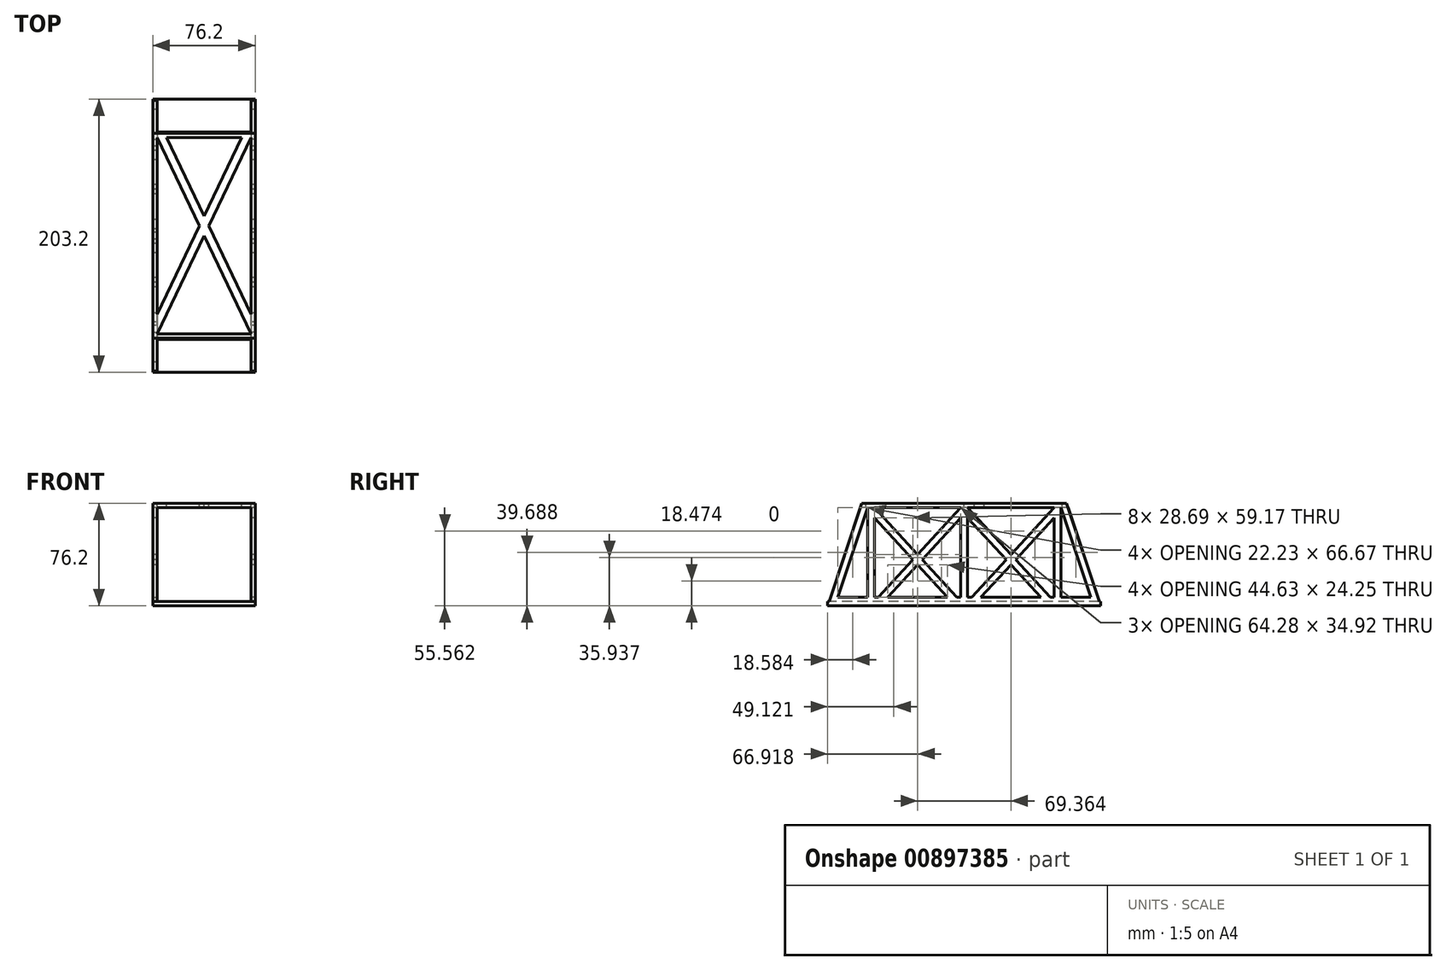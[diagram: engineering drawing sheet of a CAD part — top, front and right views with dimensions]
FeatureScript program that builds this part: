
annotation { "Feature Type Name" : "Feature", "Feature Type Description" : "" }
export const myFeature = defineFeature(function(context is Context, id is Id, definition is map)
    precondition{}
    {
        {
            var Q0;
            Q0=qCreatedBy(makeId("Right.planeOp"),FACE);
            var sketch = newSketch(context, id + "F0", { "sketchPlane" : qUnion([Q0])});
            skLineSegment(sketch, "E0", {"start": v(-101.6, -38.1) * mm, "end": v(101.6, -38.1) * mm});
            skLineSegment(sketch, "E1", {"start": v(101.6, -38.1) * mm, "end": v(76.2, 38.1) * mm});
            skLineSegment(sketch, "E2", {"start": v(76.2, 38.1) * mm, "end": v(-76.2, 38.1) * mm});
            skLineSegment(sketch, "E3", {"start": v(-76.2, 38.1) * mm, "end": v(-101.6, -38.1) * mm});
            skSolve(sketch);
        }
        {
            var Q0;
            Q0 = qSketchRegion(id + "F0", true);
            extrude(context, id + "F1", {"entities" : qUnion([Q0]), "endBound" : BoundingType.SYMMETRIC, "depth" : 76.2 * mm, "offsetDistance" : 25.4 * mm});
        }
        {
            var Q0;
            Q0=qCreatedBy(makeId("Front.planeOp"),FACE);
            var sketch = newSketch(context, id + "F2", { "sketchPlane" : qUnion([Q0])});
            skLineSegment(sketch, "E4.bottom", {"start": v(34.92, -34.93) * mm, "end": v(-34.93, -34.93) * mm});
            skLineSegment(sketch, "E4.top", {"start": v(34.92, 34.93) * mm, "end": v(-34.93, 34.92) * mm});
            skLineSegment(sketch, "E4.left", {"start": v(34.92, -34.93) * mm, "end": v(34.92, 34.92) * mm});
            skLineSegment(sketch, "E4.right", {"start": v(-34.93, -34.93) * mm, "end": v(-34.93, 34.92) * mm});
            skPoint(sketch, "E4.middle", {"position": v(0, 0) * mm});
            skSolve(sketch);
        }
        {
            var Q0;
            Q0 = qSketchRegion(id + "F2", true);
            extrude(context, id + "F3", {"entities" : qUnion([Q0]), "operationType" : NewBodyOperationType.REMOVE, "endBound" : BoundingType.SYMMETRIC, "oppositeDirection" : true, "depth" : 254 * mm, "offsetDistance" : 25.4 * mm});
        }
        {
            var Q0;
            Q0=makeQuery(id+"F1.opExtrude","CAP_FACE",FACE,{"disambiguationData":[OSD([sQuery(id+"F0.wireOp",EDGE,"E0"),sQuery(id+"F0.wireOp",EDGE,"E1"),sQuery(id+"F0.wireOp",EDGE,"E2"),sQuery(id+"F0.wireOp",EDGE,"E3")])],"isStart":true});
            var sketch = newSketch(context, id + "F4", { "sketchPlane" : qUnion([Q0])});
            skLineSegment(sketch, "E5", {"start": v(-95.19, -34.93) * mm, "end": v(-71.9, 34.93) * mm});
            skLineSegment(sketch, "E6", {"start": v(-71.9, 34.93) * mm, "end": v(-71.9, -34.92) * mm});
            skLineSegment(sketch, "E7", {"start": v(-71.9, -34.92) * mm, "end": v(-95.19, -34.92) * mm});
            skLineSegment(sketch, "E8.MirrorCS", {"start": v(71.9, 34.93) * mm, "end": v(71.9, -34.92) * mm});
            skLineSegment(sketch, "E9.MirrorCS", {"start": v(71.9, -34.92) * mm, "end": v(95.19, -34.92) * mm});
            skLineSegment(sketch, "E10.MirrorCS", {"start": v(95.19, -34.93) * mm, "end": v(71.9, 34.93) * mm});
            skLineSegment(sketch, "E11", {"start": v(-71.9, 34.93) * mm, "end": v(71.9, 34.93) * mm});
            skLineSegment(sketch, "E12", {"start": v(-71.9, -34.92) * mm, "end": v(71.9, -34.92) * mm});
            skLineSegment(sketch, "E13", {"start": v(-66.82, 34.93) * mm, "end": v(-66.82, -34.93) * mm});
            skLineSegment(sketch, "E14", {"start": v(66.82, 34.93) * mm, "end": v(66.82, -34.92) * mm});
            skLineSegment(sketch, "E15.bottom", {"start": v(2.54, -34.93) * mm, "end": v(-2.54, -34.93) * mm});
            skLineSegment(sketch, "E15.top", {"start": v(2.54, 34.93) * mm, "end": v(-2.54, 34.93) * mm});
            skLineSegment(sketch, "E15.left", {"start": v(2.54, -34.93) * mm, "end": v(2.54, 34.93) * mm});
            skLineSegment(sketch, "E15.right", {"start": v(-2.54, -34.93) * mm, "end": v(-2.54, 34.93) * mm});
            skPoint(sketch, "E15.middle", {"position": v(0, 0) * mm});
            skLineSegment(sketch, "E16", {"start": v(-66.82, 34.93) * mm, "end": v(-2.54, -34.93) * mm});
            skLineSegment(sketch, "E17", {"start": v(66.82, 34.93) * mm, "end": v(2.54, -34.93) * mm});
            skLineSegment(sketch, "E18", {"start": v(-66.82, 27.42) * mm, "end": v(-9.44, -34.93) * mm});
            skLineSegment(sketch, "E19", {"start": v(66.82, 27.42) * mm, "end": v(9.44, -34.93) * mm});
            skLineSegment(sketch, "E20", {"start": v(-2.54, 34.93) * mm, "end": v(-66.82, -34.93) * mm});
            skLineSegment(sketch, "E21", {"start": v(-2.54, 27.42) * mm, "end": v(-59.92, -34.93) * mm});
            skLineSegment(sketch, "E22.MirrorCS", {"start": v(2.54, 34.93) * mm, "end": v(66.82, -34.93) * mm});
            skLineSegment(sketch, "E23.MirrorCS", {"start": v(2.54, 27.42) * mm, "end": v(59.92, -34.93) * mm});
            skSolve(sketch);
        }
        {
            var Q0;
            Q0=makeQuery(id+"F4.imprint","IMPRINT",FACE,{"disambiguationData":[TD([[makeQuery(id+"F4.imprint","IMPRINT",EDGE,{"derivedFrom":sQuery(id+"F4.wireOp",EDGE,"E5")}),-1.0]])]});
            var Q1;
            {var subQ1=sQuery(id+"F4.wireOp",EDGE,"E13");var subQ3=sQuery(id+"F4.wireOp",EDGE,"E18");var subQ4=makeQuery(id+"F4.imprint","INTERSECT",VERTEX,{"derivedFrom":[subQ1,subQ3]});Q1=makeQuery(id+"F4.imprint","IMPRINT",FACE,{"disambiguationData":[TD([[makeQuery(id+"F4.imprint","IMPRINT",EDGE,{"disambiguationData":[TD([[subQ4,-1.0]])],"derivedFrom":subQ3}),-1.0]])]});}
            var Q2;
            {var subQ0=sQuery(id+"F4.wireOp",EDGE,"E16");var subQ3=sQuery(id+"F4.wireOp",EDGE,"E20");var subQ5=makeQuery(id+"F4.imprint","INTERSECT",VERTEX,{"derivedFrom":[subQ0,subQ3]});Q2=makeQuery(id+"F4.imprint","IMPRINT",FACE,{"disambiguationData":[TD([[makeQuery(id+"F4.imprint","IMPRINT",EDGE,{"disambiguationData":[TD([[subQ5,1.0]])],"derivedFrom":subQ0}),1.0]])]});}
            var Q3;
            {var subQ1=sQuery(id+"F4.wireOp",EDGE,"E15.right");var subQ3=sQuery(id+"F4.wireOp",EDGE,"E21");var subQ4=makeQuery(id+"F4.imprint","INTERSECT",VERTEX,{"derivedFrom":[subQ1,subQ3]});Q3=makeQuery(id+"F4.imprint","IMPRINT",FACE,{"disambiguationData":[TD([[makeQuery(id+"F4.imprint","IMPRINT",EDGE,{"disambiguationData":[TD([[subQ4,-1.0]])],"derivedFrom":subQ3}),1.0]])]});}
            var Q4;
            {var subQ0=sQuery(id+"F4.wireOp",EDGE,"E18");var subQ1=sQuery(id+"F4.wireOp",EDGE,"E12");var subQ2=makeQuery(id+"F4.imprint","INTERSECT",VERTEX,{"derivedFrom":[subQ1,subQ0]});Q4=makeQuery(id+"F4.imprint","IMPRINT",FACE,{"disambiguationData":[TD([[makeQuery(id+"F4.imprint","IMPRINT",EDGE,{"disambiguationData":[TD([[subQ2,1.0]])],"derivedFrom":subQ1}),1.0]])]});}
            var Q5;
            {var subQ1=sQuery(id+"F4.wireOp",EDGE,"E15.left");var subQ3=sQuery(id+"F4.wireOp",EDGE,"E23.MirrorCS");var subQ4=makeQuery(id+"F4.imprint","INTERSECT",VERTEX,{"derivedFrom":[subQ1,subQ3]});Q5=makeQuery(id+"F4.imprint","IMPRINT",FACE,{"disambiguationData":[TD([[makeQuery(id+"F4.imprint","IMPRINT",EDGE,{"disambiguationData":[TD([[subQ4,-1.0]])],"derivedFrom":subQ3}),-1.0]])]});}
            var Q6;
            {var subQ0=sQuery(id+"F4.wireOp",EDGE,"E17");var subQ3=sQuery(id+"F4.wireOp",EDGE,"E22.MirrorCS");var subQ5=makeQuery(id+"F4.imprint","INTERSECT",VERTEX,{"derivedFrom":[subQ0,subQ3]});Q6=makeQuery(id+"F4.imprint","IMPRINT",FACE,{"disambiguationData":[TD([[makeQuery(id+"F4.imprint","IMPRINT",EDGE,{"disambiguationData":[TD([[subQ5,1.0]])],"derivedFrom":subQ0}),-1.0]])]});}
            var Q7;
            {var subQ1=sQuery(id+"F4.wireOp",EDGE,"E14");var subQ3=sQuery(id+"F4.wireOp",EDGE,"E19");var subQ4=makeQuery(id+"F4.imprint","INTERSECT",VERTEX,{"derivedFrom":[subQ1,subQ3]});Q7=makeQuery(id+"F4.imprint","IMPRINT",FACE,{"disambiguationData":[TD([[makeQuery(id+"F4.imprint","IMPRINT",EDGE,{"disambiguationData":[TD([[subQ4,-1.0]])],"derivedFrom":subQ3}),1.0]])]});}
            var Q8;
            {var subQ0=sQuery(id+"F4.wireOp",EDGE,"E19");var subQ1=sQuery(id+"F4.wireOp",EDGE,"E12");var subQ2=makeQuery(id+"F4.imprint","INTERSECT",VERTEX,{"derivedFrom":[subQ1,subQ0]});Q8=makeQuery(id+"F4.imprint","IMPRINT",FACE,{"disambiguationData":[TD([[makeQuery(id+"F4.imprint","IMPRINT",EDGE,{"disambiguationData":[TD([[subQ2,-1.0]])],"derivedFrom":subQ1}),1.0]])]});}
            var Q9;
            Q9=makeQuery(id+"F4.imprint","IMPRINT",FACE,{"disambiguationData":[TD([[makeQuery(id+"F4.imprint","IMPRINT",EDGE,{"derivedFrom":sQuery(id+"F4.wireOp",EDGE,"E8.MirrorCS")}),1.0]])]});
            extrude(context, id + "F5", {"entities" : qUnion([Q0, Q1, Q2, Q3, Q4, Q5, Q6, Q7, Q8, Q9]), "operationType" : NewBodyOperationType.REMOVE, "oppositeDirection" : true, "depth" : 76.2 * mm, "offsetDistance" : 25.4 * mm});
        }
        {
            var Q0;
            Q0=makeQuery(id+"F1.opExtrude","SWEPT_FACE",FACE,{"disambiguationData":[OSD([sQuery(id+"F0.wireOp",EDGE,"E2")])]});
            var sketch = newSketch(context, id + "F6", { "sketchPlane" : qUnion([Q0])});
            skLineSegment(sketch, "E24.bottom", {"start": v(34.92, -73.03) * mm, "end": v(-34.93, -73.03) * mm});
            skLineSegment(sketch, "E24.top", {"start": v(34.92, 73.03) * mm, "end": v(-34.92, 73.03) * mm});
            skLineSegment(sketch, "E24.left", {"start": v(34.92, -73.03) * mm, "end": v(34.93, 73.02) * mm});
            skLineSegment(sketch, "E24.right", {"start": v(-34.93, -73.03) * mm, "end": v(-34.92, 73.02) * mm});
            skPoint(sketch, "E24.middle", {"position": v(0, 0) * mm});
            skLineSegment(sketch, "E25", {"start": v(-34.92, 73.03) * mm, "end": v(34.92, -73.03) * mm});
            skLineSegment(sketch, "E26", {"start": v(34.92, 73.03) * mm, "end": v(-34.92, -73.03) * mm});
            skLineSegment(sketch, "E27", {"start": v(27.89, 73.03) * mm, "end": v(-34.93, -58.3) * mm});
            skLineSegment(sketch, "E28", {"start": v(-27.89, 73.02) * mm, "end": v(34.93, -58.3) * mm});
            skSolve(sketch);
        }
        {
            var Q0;
            {var subQ1=sQuery(id+"F6.wireOp",EDGE,"E24.right");var subQ3=sQuery(id+"F6.wireOp",EDGE,"E27");var subQ4=makeQuery(id+"F6.imprint","INTERSECT",VERTEX,{"derivedFrom":[subQ1,subQ3]});Q0=makeQuery(id+"F6.imprint","IMPRINT",FACE,{"disambiguationData":[TD([[makeQuery(id+"F6.imprint","IMPRINT",EDGE,{"disambiguationData":[TD([[subQ4,1.0]])],"derivedFrom":subQ3}),-1.0]])]});}
            var Q1;
            {var subQ0=sQuery(id+"F6.wireOp",EDGE,"E24.bottom");Q1=makeQuery(id+"F6.imprint","IMPRINT",FACE,{"disambiguationData":[TD([[makeQuery(id+"F6.imprint","IMPRINT",EDGE,{"derivedFrom":subQ0}),-1.0]])]});}
            var Q2;
            {var subQ1=sQuery(id+"F6.wireOp",EDGE,"E24.left");var subQ3=sQuery(id+"F6.wireOp",EDGE,"E28");var subQ4=makeQuery(id+"F6.imprint","INTERSECT",VERTEX,{"derivedFrom":[subQ1,subQ3]});Q2=makeQuery(id+"F6.imprint","IMPRINT",FACE,{"disambiguationData":[TD([[makeQuery(id+"F6.imprint","IMPRINT",EDGE,{"disambiguationData":[TD([[subQ4,1.0]])],"derivedFrom":subQ3}),1.0]])]});}
            var Q3;
            {var subQ0=sQuery(id+"F6.wireOp",EDGE,"E27");var subQ1=sQuery(id+"F6.wireOp",EDGE,"E24.top");var subQ2=makeQuery(id+"F6.imprint","INTERSECT",VERTEX,{"derivedFrom":[subQ1,subQ0]});Q3=makeQuery(id+"F6.imprint","IMPRINT",FACE,{"disambiguationData":[TD([[makeQuery(id+"F6.imprint","IMPRINT",EDGE,{"disambiguationData":[TD([[subQ2,-1.0]])],"derivedFrom":subQ1}),1.0]])]});}
            extrude(context, id + "F7", {"entities" : qUnion([Q0, Q1, Q2, Q3]), "operationType" : NewBodyOperationType.REMOVE, "oppositeDirection" : true, "depth" : 25.4 * mm, "offsetDistance" : 25.4 * mm});
        }
        {
            var Q0;
            {var subQ0=sQuery(id+"F4.wireOp",EDGE,"E12");Q0=makeQuery(id+"F5.boolean.opBoolean","MERGE",FACE,{"derivedFrom":[makeQuery(id+"F3.boolean.opBoolean","COPY",FACE,{"derivedFrom":makeQuery(id+"F3.opExtrude","SWEPT_FACE",FACE,{"disambiguationData":[OSD([sQuery(id+"F2.wireOp",EDGE,"E4.bottom")])]})})],"fromTools":[makeQuery(id+"F5.opExtrude","SWEPT_FACE",FACE,{"disambiguationData":[OSD([sQuery(id+"F4.wireOp",EDGE,"E7")])]}),makeQuery(id+"F5.opExtrude","SWEPT_FACE",FACE,{"disambiguationData":[OSD([sQuery(id+"F4.wireOp",EDGE,"E9.MirrorCS")])]}),makeQuery(id+"F5.opExtrude","SWEPT_FACE",FACE,{"disambiguationData":[OSD([subQ0]),TDD([makeQuery(id+"F4.imprint","IMPRINT",EDGE,{"disambiguationData":[TD([[makeQuery(id+"F4.imprint","INTERSECT",VERTEX,{"derivedFrom":[subQ0,sQuery(id+"F4.wireOp",EDGE,"E18")]}),1.0]])],"derivedFrom":subQ0})])]}),makeQuery(id+"F5.opExtrude","SWEPT_FACE",FACE,{"disambiguationData":[OSD([subQ0]),TDD([makeQuery(id+"F4.imprint","IMPRINT",EDGE,{"disambiguationData":[TD([[makeQuery(id+"F4.imprint","INTERSECT",VERTEX,{"derivedFrom":[subQ0,sQuery(id+"F4.wireOp",EDGE,"E19")]}),-1.0]])],"derivedFrom":subQ0})])]})]});}
            var sketch = newSketch(context, id + "F8", { "sketchPlane" : qUnion([Q0])});
            skLineSegment(sketch, "E29.bottom", {"start": v(-38.1, -95.19) * mm, "end": v(-34.93, -95.19) * mm});
            skLineSegment(sketch, "E29.top", {"start": v(-38.1, 95.19) * mm, "end": v(-34.93, 95.19) * mm});
            skLineSegment(sketch, "E29.left", {"start": v(-38.1, -95.19) * mm, "end": v(-38.1, 95.19) * mm});
            skLineSegment(sketch, "E29.right", {"start": v(-34.93, -95.19) * mm, "end": v(-34.93, 95.19) * mm});
            skLineSegment(sketch, "E30.MirrorCS", {"start": v(38.1, -95.19) * mm, "end": v(34.93, -95.19) * mm});
            skLineSegment(sketch, "E31.MirrorCS", {"start": v(38.1, -95.19) * mm, "end": v(38.1, 95.19) * mm});
            skLineSegment(sketch, "E32.MirrorCS", {"start": v(34.93, -95.19) * mm, "end": v(34.93, 95.19) * mm});
            skLineSegment(sketch, "E33.MirrorCS", {"start": v(38.1, 95.19) * mm, "end": v(34.93, 95.19) * mm});
            skSolve(sketch);
        }
        {
            var Q0;
            Q0 = qSketchRegion(id + "F8", true);
            extrude(context, id + "F9", {"entities" : qUnion([Q0]), "operationType" : NewBodyOperationType.ADD, "depth" : 3.17 * mm, "offsetDistance" : 25.4 * mm});
        }
        {
            var Q0;
            Q0=makeQuery(id+"F9.boolean.opBoolean","MERGE",FACE,{"derivedFrom":[makeQuery(id+"F1.opExtrude","CAP_FACE",FACE,{"disambiguationData":[OSD([sQuery(id+"F0.wireOp",EDGE,"E0"),sQuery(id+"F0.wireOp",EDGE,"E1"),sQuery(id+"F0.wireOp",EDGE,"E2"),sQuery(id+"F0.wireOp",EDGE,"E3")])],"isStart":false}),makeQuery(id+"F9.opExtrude","SWEPT_FACE",FACE,{"disambiguationData":[OSD([sQuery(id+"F8.wireOp",EDGE,"E31.MirrorCS")])]})]});
            var sketch = newSketch(context, id + "F10", { "sketchPlane" : qUnion([Q0])});
            skLineSegment(sketch, "E34.bottom", {"start": v(-101.6, -38.1) * mm, "end": v(-97.33, -38.1) * mm});
            skLineSegment(sketch, "E34.top", {"start": v(-101.6, -34.93) * mm, "end": v(-97.33, -34.93) * mm});
            skLineSegment(sketch, "E34.left", {"start": v(-101.6, -38.1) * mm, "end": v(-101.6, -34.93) * mm});
            skLineSegment(sketch, "E34.right", {"start": v(-97.33, -38.1) * mm, "end": v(-97.33, -34.93) * mm});
            skLineSegment(sketch, "E35.MirrorCS", {"start": v(97.33, -38.1) * mm, "end": v(97.33, -34.93) * mm});
            skLineSegment(sketch, "E36.MirrorCS", {"start": v(101.6, -34.93) * mm, "end": v(97.33, -34.93) * mm});
            skLineSegment(sketch, "E37.MirrorCS", {"start": v(101.6, -38.1) * mm, "end": v(101.6, -34.93) * mm});
            skLineSegment(sketch, "E38.MirrorCS", {"start": v(101.6, -38.1) * mm, "end": v(97.33, -38.1) * mm});
            skSolve(sketch);
        }
        {
            var Q0;
            Q0 = qSketchRegion(id + "F10", true);
            extrude(context, id + "F11", {"entities" : qUnion([Q0]), "operationType" : NewBodyOperationType.ADD, "oppositeDirection" : true, "depth" : 76.2 * mm, "offsetDistance" : 25.4 * mm});
        }
    });
